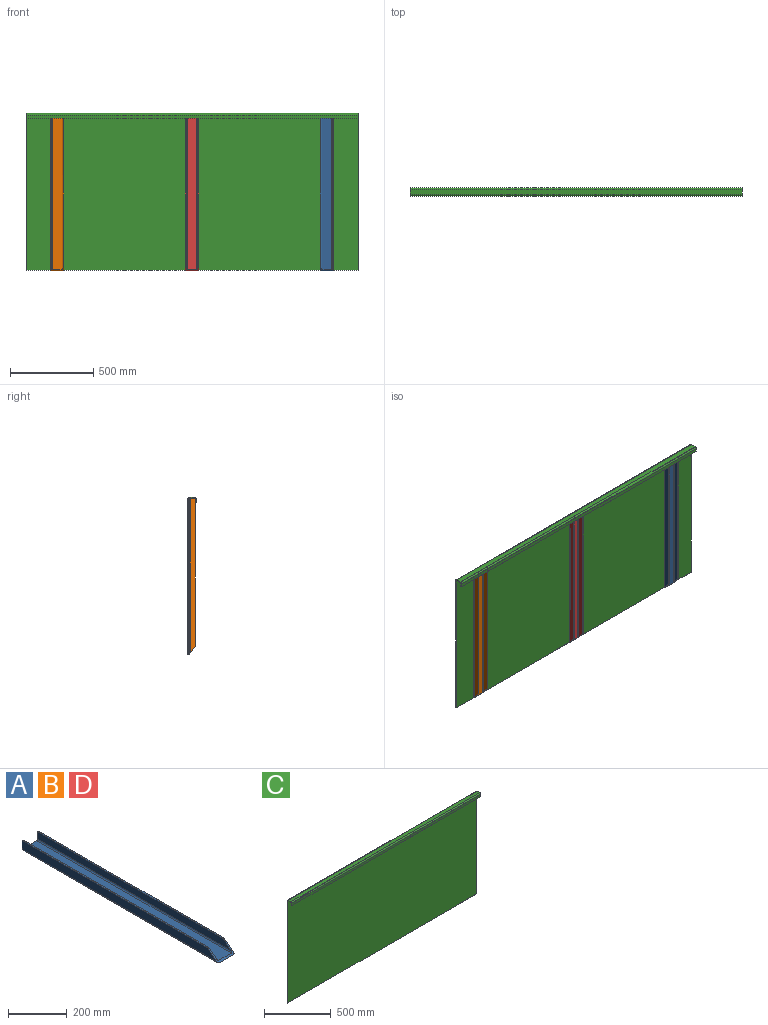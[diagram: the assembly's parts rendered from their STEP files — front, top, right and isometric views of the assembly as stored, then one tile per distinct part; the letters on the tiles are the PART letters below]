
ASSEMBLY  parts=4 mates=3
PART A: 14 faces, bbox 80x940x40 mm
  f0: plane 890x5mm, normal (0,0,1), area 4450mm2, adj f3,f4,f7,f13
  f1: plane 890x5mm, normal (0,0,1), area 4450mm2, adj f4,f5,f8,f13
  f2: plane 933.75x60mm, normal (0,0,1), area 56025mm2, adj f4,f9,f10,f13
  f3: plane 933.75x35mm, normal (1,0,0), area 31915.6mm2, adj f0,f4,f12,f13
  f4: plane 80x40mm, normal (0,1,0), area 750mm2, adj f0,f1,f2,f3,f5,f6,f7,f8
  f5: plane 933.75x35mm, normal (-1,0,0), area 31915.6mm2, adj f1,f4,f11,f13
  f6: plane 940x70mm, normal (0,0,-1), area 65800mm2, adj f4,f11,f12,f13
  f7: plane 927.5x30mm, normal (-1,0,0), area 27262.5mm2, adj f0,f4,f10,f13
  f8: plane 927.5x30mm, normal (1,0,0), area 27262.5mm2, adj f1,f4,f9,f13
  f9: cylinder r=5mm len=933.75mm, axis (0,1,0), area 7315.8mm2, adj f2,f4,f8,f13
  f10: cylinder r=5mm len=933.75mm, axis (0,-1,0), area 7315.8mm2, adj f2,f4,f7,f13
  f11: cylinder r=5mm len=940mm, axis (0,-1,0), area 7364.9mm2, adj f4,f5,f6,f13
  f12: cylinder r=5mm len=940mm, axis (0,1,0), area 7364.9mm2, adj f3,f4,f6,f13
  f13: plane 80x50mm, normal (0,-0.62,0.78), area 1200.6mm2, adj f0,f1,f2,f3,f5,f6,f7,f8
PART B: same geometry as A
PART C: 22 faces, bbox 2000x50x945 mm
  f0: plane 935x5mm, normal (1,0,0), area 4675mm2, adj f1,f3,f4,f19
  f1: plane 2000x5mm, normal (0,0,-1), area 10000mm2, adj f0,f2,f3,f4
  f2: plane 935x5mm, normal (-1,0,0), area 4675mm2, adj f1,f3,f4,f18
  f3: plane 2000x935mm, normal (0,1,0), area 1870000mm2, adj f0,f1,f2,f20
  f4: plane 2000x935mm, normal (0,-1,0), area 1870000mm2, adj f0,f1,f2,f21
  f5: plane 30x5mm, normal (1,0,0), area 150mm2, adj f7,f8,f14,f19
  f6: plane 30x5mm, normal (-1,0,0), area 150mm2, adj f7,f8,f15,f18
  f7: plane 2000x30mm, normal (0,0,1), area 60000mm2, adj f5,f6,f16,f20
  f8: plane 2000x30mm, normal (0,0,-1), area 60000mm2, adj f5,f6,f17,f21
  f9: plane 2000x5mm, normal (0,0,-1), area 10000mm2, adj f10,f11,f12,f13
  f10: plane 20x5mm, normal (1,0,0), area 100mm2, adj f9,f12,f13,f14
  f11: plane 20x5mm, normal (-1,0,0), area 100mm2, adj f9,f12,f13,f15
  f12: plane 2000x20mm, normal (0,-1,0), area 40000mm2, adj f9,f10,f11,f16
  f13: plane 2000x20mm, normal (0,1,0), area 40000mm2, adj f9,f10,f11,f17
  f14: plane 10x10mm, normal (1,0,0), area 58.9mm2, adj f5,f10,f16,f17
  f15: plane 10x10mm, normal (-1,0,0), area 58.9mm2, adj f6,f11,f16,f17
  f16: cylinder r=10mm len=2000mm, axis (1,0,0), area 31415.9mm2, adj f7,f12,f14,f15
  f17: cylinder r=5mm len=2000mm, axis (1,0,0), area 15708mm2, adj f8,f13,f14,f15
  f18: plane 10x10mm, normal (-1,0,0), area 58.9mm2, adj f2,f6,f20,f21
  f19: plane 10x10mm, normal (1,0,0), area 58.9mm2, adj f0,f5,f20,f21
  f20: cylinder r=10mm len=2000mm, axis (-1,0,0), area 31415.9mm2, adj f3,f7,f18,f19
  f21: cylinder r=5mm len=2000mm, axis (-1,0,0), area 15708mm2, adj f4,f8,f18,f19
PART D: same geometry as A
PLACE A rot(axis=(1,0,0),90deg) t=(771.69,-22.84,-34.35)mm
PLACE B rot(axis=(1,0,0),90deg) t=(-852.31,-22.84,-34.35)mm
PLACE C t=(-40.31,-17.84,-29.35)mm fixed
PLACE D rot(axis=(1,0,0),90deg) t=(-40.31,-22.84,-34.35)mm
MATE fastened A.f6 <-> C.f4  axis (0,1,0) through (771.69,-22.84,-34.35)mm
MATE fastened D.f6 <-> C.f4  axis (0,1,0) through (-40.31,-22.84,-34.35)mm
MATE fastened B.f6 <-> C.f4  axis (0,1,0) through (-852.31,-22.84,-34.35)mm
